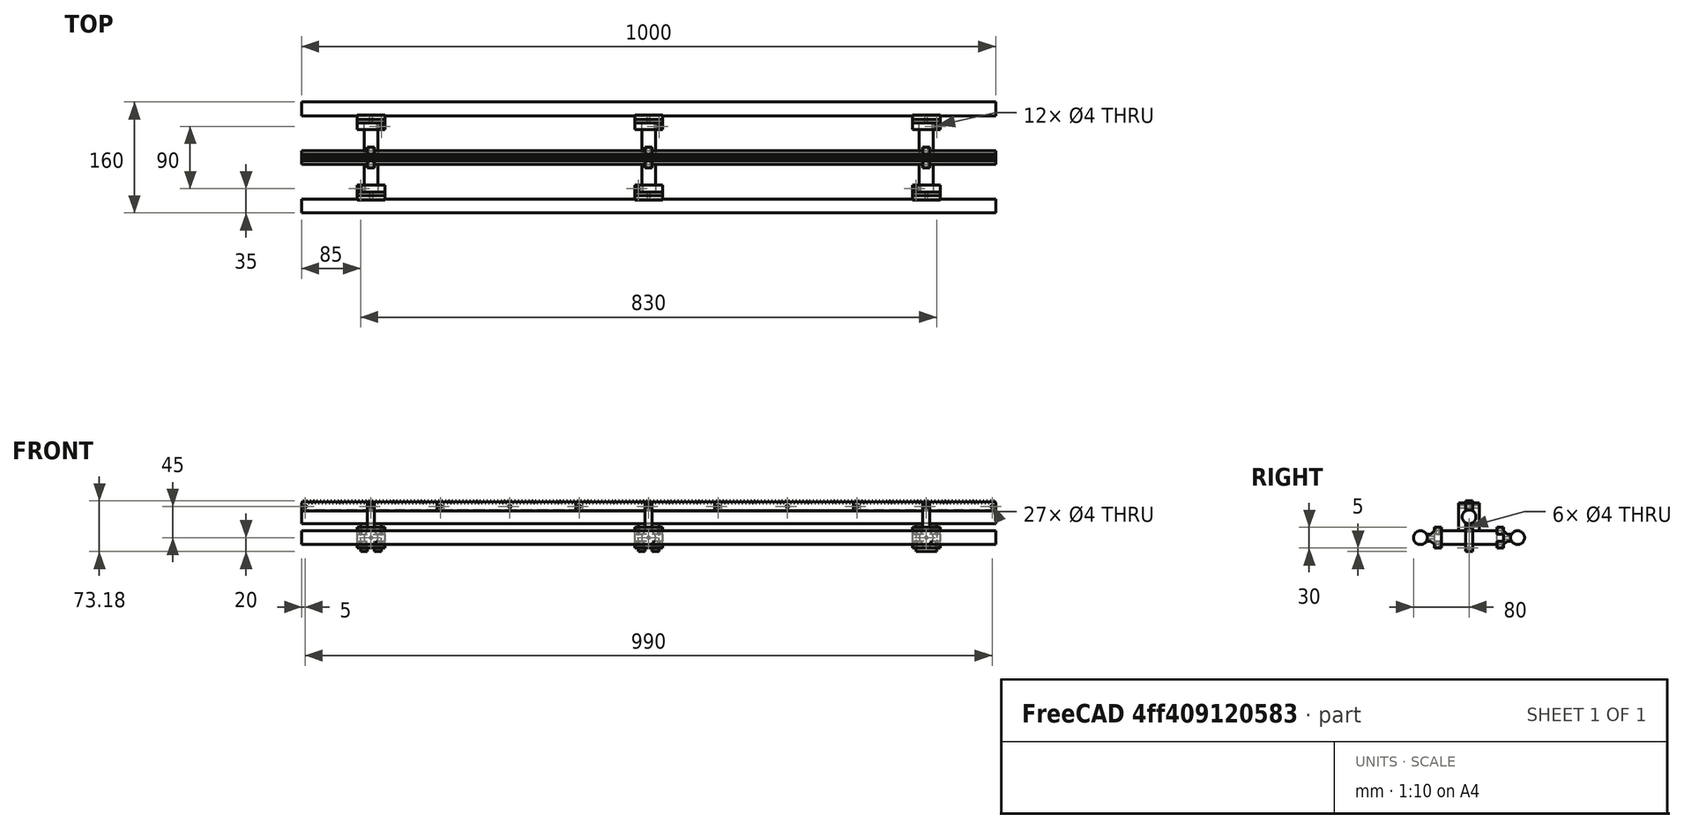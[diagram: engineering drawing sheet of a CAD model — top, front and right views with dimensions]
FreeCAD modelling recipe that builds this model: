
FCSTD DOCUMENT  (FreeCAD 0.17R13522 (Git))
Label: rail
License: All rights reserved
LicenseURL: http://en.wikipedia.org/wiki/All_rights_reserved
objects: Part::FeaturePython×17, Part::Cylinder×6, Part::Compound×5
note: 28 computed .brp shape members not serialized (recipe doc carries the construction recipe); baked Part::Feature solids carry a one-line shape summary decoded from their .brp

FEATURE [Part::FeaturePython] rack_003  # a2plus imported part (geometry in sourceFile) (typed FeaturePython)
  Placement = pos=(305,0,40) rot=(0.57735,-0.57735,0.57735;2.0944rad)
  fixedPosition = true
  sourceFile = <userpath>/repo/mavis/parts/rack.fcstd
  timeLastImport = 1.53613e+09
  updateColors = true
FEATURE [Part::FeaturePython] rack_004  # a2plus imported part (geometry in sourceFile) (typed FeaturePython)
  Placement = pos=(105,0,40) rot=(0.57735,-0.57735,0.57735;2.0944rad)
  fixedPosition = true
  sourceFile = <userpath>/repo/mavis/parts/rack.fcstd
  timeLastImport = 1.53613e+09
  updateColors = true
FEATURE [Part::FeaturePython] rack_005  # a2plus imported part (geometry in sourceFile) (typed FeaturePython)
  Placement = pos=(-95,0,40) rot=(0.57735,-0.57735,0.57735;2.0944rad)
  fixedPosition = true
  sourceFile = <userpath>/repo/mavis/parts/rack.fcstd
  timeLastImport = 1.53613e+09
  updateColors = true
FEATURE [Part::FeaturePython] fastener_01  # a2plus imported part (geometry in sourceFile) (typed FeaturePython)
  Placement = pos=(0,0,30) rot=(0,1,0;1.5708rad)
  fixedPosition = false
  sourceFile = <userpath>/repo/mavis/parts/fastener-join-20mm.fcstd
  timeLastImport = 1.53606e+09
  updateColors = true
FEATURE [Part::FeaturePython] fastener_002  # a2plus imported part (geometry in sourceFile) (typed FeaturePython)
  Placement = pos=(400,0,30) rot=(0,1,0;1.5708rad)
  fixedPosition = false
  sourceFile = <userpath>/repo/mavis/parts/fastener-join-20mm.fcstd
  timeLastImport = 1.53606e+09
  updateColors = true
FEATURE [Part::FeaturePython] fastener_003  # a2plus imported part (geometry in sourceFile) (typed FeaturePython)
  Placement = pos=(400,0,0) rot=(0.57735,-0.57735,-0.57735;4.18879rad)
  fixedPosition = false
  sourceFile = <userpath>/repo/mavis/parts/fastener-join-20mm.fcstd
  timeLastImport = 1.53606e+09
  updateColors = true
FEATURE [Part::FeaturePython] fastener_004  # a2plus imported part (geometry in sourceFile) (typed FeaturePython)
  Placement = pos=(-400,0,30) rot=(0,1,0;1.5708rad)
  fixedPosition = false
  sourceFile = <userpath>/repo/mavis/parts/fastener-join-20mm.fcstd
  timeLastImport = 1.53606e+09
  updateColors = true
FEATURE [Part::FeaturePython] fastener_005  # a2plus imported part (geometry in sourceFile) (typed FeaturePython)
  Placement = pos=(-400,0,0) rot=(0.57735,0.57735,0.57735;4.18879rad)
  fixedPosition = false
  sourceFile = <userpath>/repo/mavis/parts/fastener-join-20mm.fcstd
  timeLastImport = 1.53606e+09
  updateColors = true
FEATURE [Part::FeaturePython] fastener_006  # a2plus imported part (geometry in sourceFile) (typed FeaturePython)
  Placement = pos=(0,0,0) rot=(0.57735,0.57735,0.57735;4.18879rad)
  fixedPosition = false
  sourceFile = <userpath>/repo/mavis/parts/fastener-join-20mm.fcstd
  timeLastImport = 1.53606e+09
  updateColors = true
FEATURE [Part::FeaturePython] sleeperinner_01  # a2plus imported part (geometry in sourceFile) (typed FeaturePython)
  Placement = pos=(400,45,0) rot=(0,0.707107,0.707107;3.14159rad)
  fixedPosition = false
  sourceFile = <userpath>/repo/mavis/parts/sleeperinner.fcstd
  timeLastImport = 1.53613e+09
  updateColors = true
FEATURE [Part::FeaturePython] sleeperinner_002  # a2plus imported part (geometry in sourceFile) (typed FeaturePython)
  Placement = pos=(-400,-45,0) rot=(1,0,0;1.5708rad)
  fixedPosition = false
  sourceFile = <userpath>/repo/mavis/parts/sleeperinner.fcstd
  timeLastImport = 1.53613e+09
  updateColors = true
FEATURE [Part::FeaturePython] sleeperinner_003  # a2plus imported part (geometry in sourceFile) (typed FeaturePython)
  Placement = pos=(400,-45,0) rot=(1,0,0;1.5708rad)
  fixedPosition = false
  sourceFile = <userpath>/repo/mavis/parts/sleeperinner.fcstd
  timeLastImport = 1.53613e+09
  updateColors = true
FEATURE [Part::FeaturePython] sleeperinner_004  # a2plus imported part (geometry in sourceFile) (typed FeaturePython)
  Placement = pos=(0,-45,0) rot=(1,0,0;1.5708rad)
  fixedPosition = false
  sourceFile = <userpath>/repo/mavis/parts/sleeperinner.fcstd
  timeLastImport = 1.53613e+09
  updateColors = true
FEATURE [Part::FeaturePython] sleeperinner_005  # a2plus imported part (geometry in sourceFile) (typed FeaturePython)
  Placement = pos=(-400,45,0) rot=(0,0.707107,0.707107;3.14159rad)
  fixedPosition = false
  sourceFile = <userpath>/repo/mavis/parts/sleeperinner.fcstd
  timeLastImport = 1.53613e+09
  updateColors = true
FEATURE [Part::FeaturePython] sleeperinner_006  # a2plus imported part (geometry in sourceFile) (typed FeaturePython)
  Placement = pos=(0,45,0) rot=(0,0.707107,0.707107;3.14159rad)
  fixedPosition = false
  sourceFile = <userpath>/repo/mavis/parts/sleeperinner.fcstd
  timeLastImport = 1.53613e+09
  updateColors = true
FEATURE [Part::Cylinder] Cylinder
  Angle = 360
  AttacherType = Attacher::AttachEngine3D
  Height = 1000
  Placement = pos=(500,70,0) rot=(0,-1,0;1.5708rad)
  Radius = 10
FEATURE [Part::Cylinder] Cylinder005
  Angle = 360
  AttacherType = Attacher::AttachEngine3D
  Height = 1000
  Placement = pos=(500,-70,0) rot=(0,-1,0;1.5708rad)
  Radius = 10
FEATURE [Part::Cylinder] Cylinder003
  Angle = 360
  AttacherType = Attacher::AttachEngine3D
  Height = 100
  Placement = pos=(0,50,0) rot=(0.57735,-0.57735,0.57735;2.0944rad)
  Radius = 10
FEATURE [Part::Cylinder] Cylinder002
  Angle = 360
  AttacherType = Attacher::AttachEngine3D
  Height = 100
  Placement = pos=(400,50,0) rot=(0.57735,-0.57735,0.57735;2.0944rad)
  Radius = 10
FEATURE [Part::Cylinder] Cylinder001
  Angle = 360
  AttacherType = Attacher::AttachEngine3D
  Height = 100
  Placement = pos=(-400,50,0) rot=(0.57735,-0.57735,0.57735;2.0944rad)
  Radius = 10
FEATURE [Part::Cylinder] Cylinder004
  Angle = 360
  AttacherType = Attacher::AttachEngine3D
  Height = 1000
  Placement = pos=(500,0,30) rot=(0,-1,0;1.5708rad)
  Radius = 10
FEATURE [Part::FeaturePython] rack_end_01  # a2plus imported part (geometry in sourceFile) (typed FeaturePython)
  Placement = pos=(-500,0,40) rot=(0.57735,0.57735,0.57735;4.18879rad)
  fixedPosition = false
  sourceFile = <userpath>/repo/mavis/parts/rack-end.fcstd
  timeLastImport = 1.53613e+09
  updateColors = true
FEATURE [Part::FeaturePython] rack_end_002  # a2plus imported part (geometry in sourceFile) (typed FeaturePython)
  Placement = pos=(500,0,40) rot=(0.57735,-0.57735,0.57735;2.0944rad)
  fixedPosition = false
  sourceFile = <userpath>/repo/mavis/parts/rack-end.fcstd
  timeLastImport = 1.53613e+09
  updateColors = true
FEATURE [Part::Compound] Compound  label="Rack Compound"
  Links = -> [rack_003,rack_005,rack_004,rack_end_01,rack_end_002]
FEATURE [Part::Compound] Compound001  label="Fastener Compound"
  Links = -> [fastener_005,fastener_004,fastener_003,fastener_002,fastener_006,fastener_01]
FEATURE [Part::Compound] Compound002  label="Sleeper Compound"
  Links = -> [sleeperinner_005,sleeperinner_003,sleeperinner_004,sleeperinner_01,sleeperinner_002,sleeperinner_006]
FEATURE [Part::Compound] Compound003  label="Rail Compound"
  Links = -> [Cylinder005,Cylinder002,Cylinder004,Cylinder001,Cylinder,Cylinder003]
FEATURE [Part::Compound] Compound004  label="Compound"
  Links = -> [Compound,Compound001,Compound002,Compound003]
